# Revit family: Canopies-USG-True_Wood-Vault
name_source: partatom
category: Specialty Equipment
revit_build: Autodesk Revit 2015 (Build: 20140903_1530(x64)
units: mm (PartAtom-declared; Revit-internal decimal feet)

## types (16) — shared parameters
Assembly Code = C3030200
Default Elevation = 0"
Description = USG True Wood Canopies
Manufacturer = USG
Radius = 144"
URL = www.usg.com

## per-type parameters (varying)
| type | Canopy Hanging Kit Height Offset | Canopy Hanging Kit Offset | Canopy Offset Constraint | Finish | Length | Model | USG Item Number | Vault Canopy 72in | Vault Canopy 96in | Width |
| 72" x 36" x 3/4" - Beech | 2 25/32" | 11/32" | 7 13/16" | Wood - USG - True Wood - Beech | 72" | WDPYHSQ3672BCH | 749132 | Yes | No | 36" |
| 72" x 36" x 3/4" - Maple | 2 25/32" | 11/32" | 7 13/16" | Wood - USG - True Wood - Maple | 72" | WDPYHSQ3672MPL | 749133 | Yes | No | 36" |
| 72" x 36" x 3/4" - Light Cherry | 2 25/32" | 11/32" | 7 13/16" | Wood - USG - True Wood - Light Cherry | 72" | WDPYHSQ3672LTC | 749134 | Yes | No | 36" |
| 72" x 36" x 3/4" - Dark Cherry | 2 25/32" | 11/32" | 7 13/16" | Wood - USG - True Wood - Dark Cherry | 72" | WDPYHSQ3672DKC | 749135 | Yes | No | 36" |
| 72" x 36" x 3/4" - Walnut | 2 25/32" | 11/32" | 7 13/16" | Wood - USG - True Wood - Walnut | 72" | WDPYHSQ3672WLN | 749136 | Yes | No | 36" |
| 72" x 36" x 3/4" - Red Oak | 2 25/32" | 11/32" | 7 13/16" | Wood - USG - True Wood - Red Oak | 72" | WDPYHSQ3672RDO | 749137 | Yes | No | 36" |
| 72" x 36" x 3/4" - Light Bamboo | 2 25/32" | 11/32" | 7 13/16" | Wood - USG - True Wood - Light Bamboo | 72" | WDPYHSQ3672LTB | 749138 | Yes | No | 36" |
| 72" x 36" x 3/4" - Dark Bamboo | 2 25/32" | 11/32" | 7 13/16" | Wood - USG - True Wood - Dark Bamboo | 72" | WDPYHSQ3672DKB | 749139 | Yes | No | 36" |
| 96" x 48" x  3/4" - Beech | 5 3/4" | 15/32" | 11 9/32" | Wood - USG - True Wood - Beech | 96" | WDPYHSQ4896BCH | 749156 | No | Yes | 48" |
| 96" x 48" x  3/4" - Maple | 5 3/4" | 15/32" | 11 9/32" | Wood - USG - True Wood - Maple | 96" | WDPYHSQ4896MPL | 749157 | No | Yes | 48" |
| 96" x 48" x  3/4" - Light Cherry | 5 3/4" | 15/32" | 11 9/32" | Wood - USG - True Wood - Light Cherry | 96" | WDPYHSQ4896LTC | 749158 | No | Yes | 48" |
| 96" x 48" x  3/4" - Dark Cherry | 5 3/4" | 15/32" | 11 9/32" | Wood - USG - True Wood - Dark Cherry | 96" | WDPYHSQ4896DKC | 749159 | No | Yes | 48" |
| 96" x 48" x  3/4" - Walnut | 5 3/4" | 15/32" | 11 9/32" | Wood - USG - True Wood - Walnut | 96" | WDPYHSQ4896WLN | 749160 | No | Yes | 48" |
| 96" x 48" x  3/4" - Red Oak | 5 3/4" | 15/32" | 11 9/32" | Wood - USG - True Wood - Red Oak | 96" | WDPYHSQ4896RDO | 749161 | No | Yes | 48" |
| 96" x 48" x  3/4" - Light Bamboo | 5 3/4" | 15/32" | 11 9/32" | Wood - USG - True Wood - Light Bamboo | 96" | WDPYHSQ4896LTB | 749162 | No | Yes | 48" |
| 96" x 48" x  3/4" - Dark Bamboo | 5 3/4" | 15/32" | 11 9/32" | Wood - USG - True Wood - Dark Bamboo | 96" | WDPYHSQ4896DKB | 749163 | No | Yes | 48" |

## geometry (parser evidence)
native form markers: Sweep x6
no freeform markers — native parametric forms only
